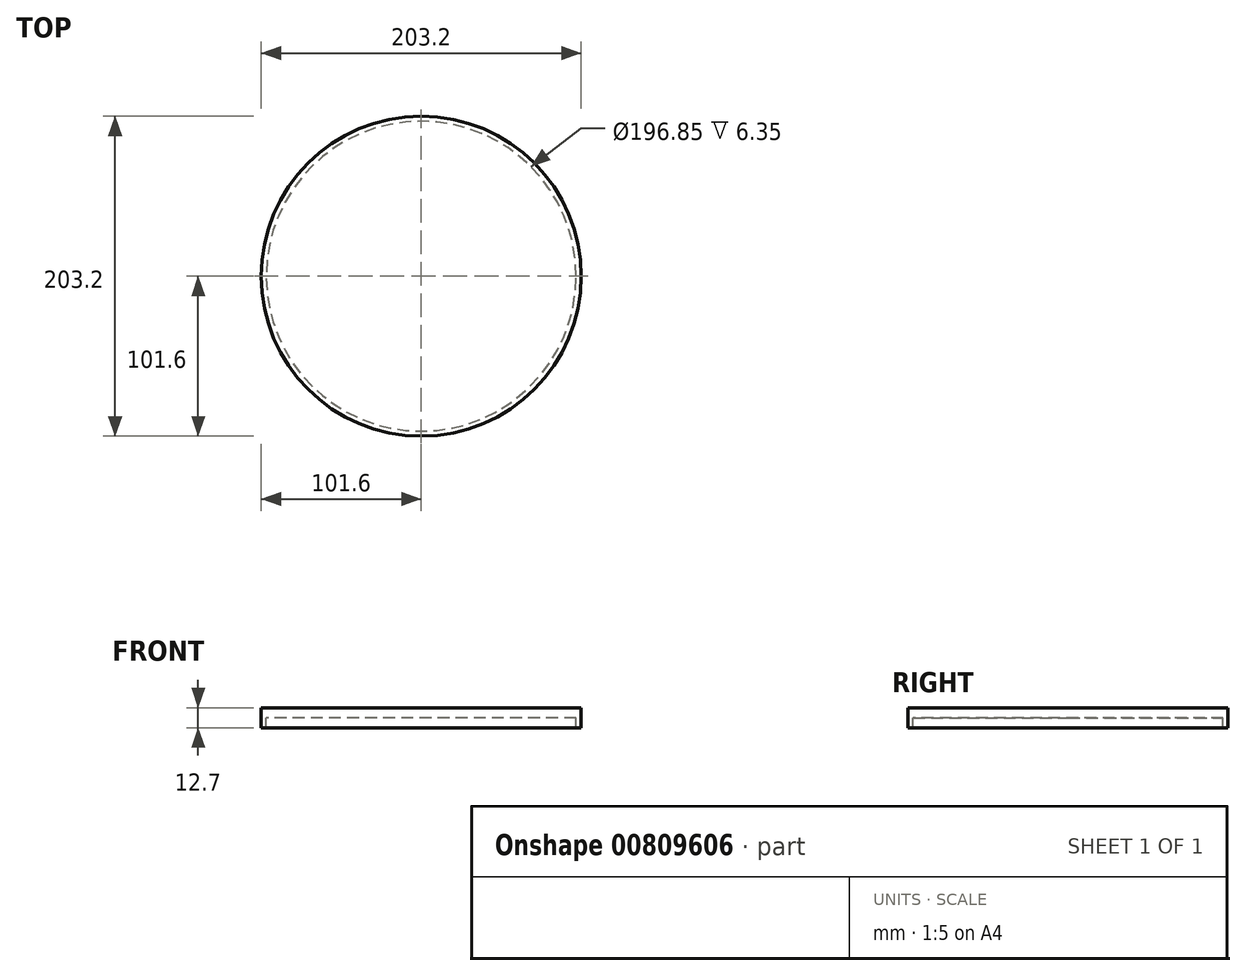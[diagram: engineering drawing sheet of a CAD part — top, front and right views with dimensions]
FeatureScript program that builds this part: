
annotation { "Feature Type Name" : "Feature", "Feature Type Description" : "" }
export const myFeature = defineFeature(function(context is Context, id is Id, definition is map)
    precondition{}
    {
        {
            var Q0;
            Q0=qCreatedBy(makeId("Top.planeOp"),FACE);
            var sketch = newSketch(context, id + "F0", { "sketchPlane" : qUnion([Q0])});
            skCircle(sketch, "E0", {"center": v(0, 0) * mm, "radius": 101.6 * mm});
            skCircle(sketch, "E1", {"center": v(0, 0) * mm, "radius": 98.43 * mm});
            skSolve(sketch);
        }
        {
            var Q0;
            Q0=makeQuery(id+"F0.imprint","IMPRINT",FACE,{"disambiguationData":[TD([[makeQuery(id+"F0.imprint","IMPRINT",EDGE,{"derivedFrom":sQuery(id+"F0.wireOp",EDGE,"E0")}),1.0]])]});
            extrude(context, id + "F1", {"entities" : qUnion([Q0]), "oppositeDirection" : true, "depth" : 12.7 * mm, "offsetDistance" : 25.4 * mm});
        }
        {
            var Q0;
            Q0=qCreatedBy(makeId("Top.planeOp"),FACE);
            var sketch = newSketch(context, id + "F2", { "sketchPlane" : qUnion([Q0])});
            skCircle(sketch, "E2", {"center": v(0, 0) * mm, "radius": 98.43 * mm});
            skSolve(sketch);
        }
        {
            var Q0;
            Q0=makeQuery(id+"F2.imprint","IMPRINT",FACE,{"disambiguationData":[TD([[makeQuery(id+"F2.imprint","IMPRINT",EDGE,{"derivedFrom":sQuery(id+"F2.wireOp",EDGE,"E2")}),1.0]])]});
            extrude(context, id + "F3", {"entities" : qUnion([Q0]), "operationType" : NewBodyOperationType.ADD, "oppositeDirection" : true, "depth" : 6.35 * mm, "offsetDistance" : 25.4 * mm});
        }
    });
